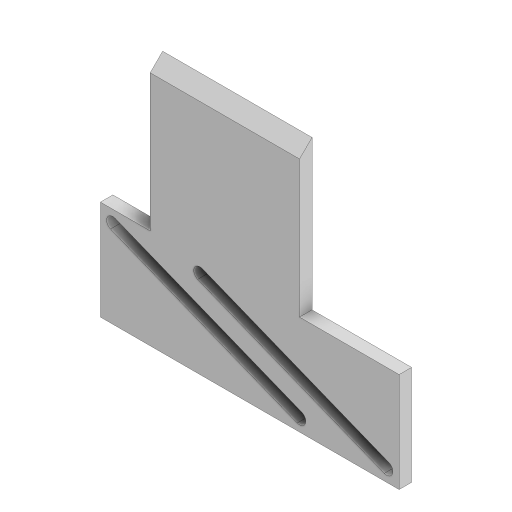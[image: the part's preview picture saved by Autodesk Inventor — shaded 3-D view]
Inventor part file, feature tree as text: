
AUTODESK INVENTOR PART (.ipt)
format: ipt  version: 2024.2 (Build 282272000, 272)  size: 124,928 bytes
history: native  units: in
note: dims shown in document units (in); Inventor stores cm internally (conversion verified against a paired STEP export)
features: extrude x1, chamfer x1, sketch x1
ambient origin geometry x8: Origin, YZ Plane, XZ Plane, XY Plane, X Axis, Y Axis, Z Axis, Center Point
bodies: Solid1 (feature_tree)
feature tree (3):
  extrude  "Extrusion1"  Depth=0.25in TaperAngle=0.0deg
  chamfer  "Chamfer1"  Distance=0.25in Angle=45.0deg
  sketch  "Sketch1"  dims[d0=3.0in d1=3.0in d2=6.0in d3=2.0in d4=1.0in d5=0.25in d6=0.25in d7=0.25in d8=0.25in d9=0.25in d10=0.25in d11=0.25in d12=0.25in d13=0.25in d14=0.0in d15=0.25in d16=0.125in d17=45.0deg]
